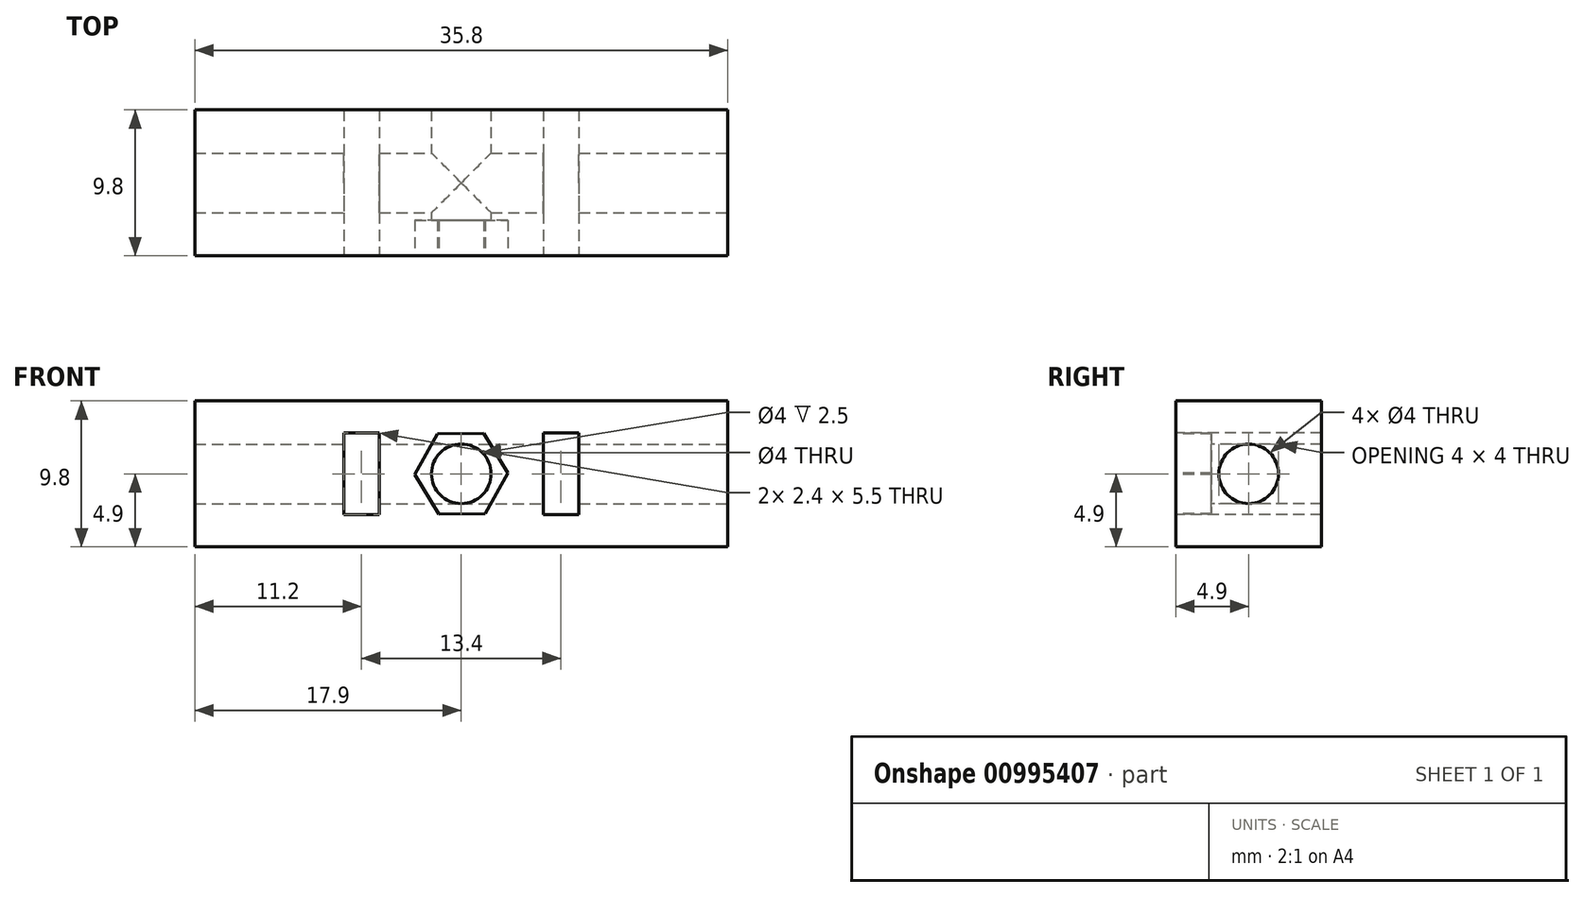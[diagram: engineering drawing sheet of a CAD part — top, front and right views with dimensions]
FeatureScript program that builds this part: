
annotation { "Feature Type Name" : "Feature", "Feature Type Description" : "" }
export const myFeature = defineFeature(function(context is Context, id is Id, definition is map)
    precondition{}
    {
        {
            var Q0;
            Q0=qCreatedBy(makeId("Front.planeOp"),FACE);
            var sketch = newSketch(context, id + "F0", { "sketchPlane" : qUnion([Q0])});
            skLineSegment(sketch, "E0.bottom", {"start": v(-17.9, 4.9) * mm, "end": v(17.9, 4.9) * mm});
            skLineSegment(sketch, "E0.top", {"start": v(-17.9, -4.9) * mm, "end": v(17.9, -4.9) * mm});
            skLineSegment(sketch, "E0.left", {"start": v(-17.9, 4.9) * mm, "end": v(-17.9, -4.9) * mm});
            skLineSegment(sketch, "E0.right", {"start": v(17.9, 4.9) * mm, "end": v(17.9, -4.9) * mm});
            skPoint(sketch, "E0.middle", {"position": v(0, 0) * mm});
            skSolve(sketch);
        }
        {
            var Q0;
            Q0=makeQuery(id+"F0.imprint","IMPRINT",FACE,{"disambiguationData":[TD([[makeQuery(id+"F0.imprint","IMPRINT",EDGE,{"derivedFrom":sQuery(id+"F0.wireOp",EDGE,"E0.bottom")}),-1.0]])]});
            extrude(context, id + "F1", {"entities" : qUnion([Q0]), "depth" : 9.8 * mm, "offsetDistance" : 25 * mm});
        }
        {
            var Q0;
            Q0=makeQuery(id+"F1.opExtrude","CAP_FACE",FACE,{"disambiguationData":[OSD([sQuery(id+"F0.wireOp",EDGE,"E0.bottom"),sQuery(id+"F0.wireOp",EDGE,"E0.top"),sQuery(id+"F0.wireOp",EDGE,"E0.left"),sQuery(id+"F0.wireOp",EDGE,"E0.right")])],"isStart":false});
            var sketch = newSketch(context, id + "F2", { "sketchPlane" : qUnion([Q0])});
            skCircle(sketch, "E1", {"center": v(0, 0) * mm, "radius": 2 * mm});
            skSolve(sketch);
        }
        {
            var Q0;
            Q0=makeQuery(id+"F2.imprint","IMPRINT",FACE,{"disambiguationData":[TD([[makeQuery(id+"F2.imprint","IMPRINT",EDGE,{"derivedFrom":sQuery(id+"F2.wireOp",EDGE,"E1")}),1.0]])]});
            extrude(context, id + "F3", {"entities" : qUnion([Q0]), "operationType" : NewBodyOperationType.REMOVE, "oppositeDirection" : true, "depth" : 25 * mm, "offsetDistance" : 25 * mm});
        }
        {
            var Q0;
            Q0=makeQuery(id+"F1.opExtrude","CAP_FACE",FACE,{"disambiguationData":[OSD([sQuery(id+"F0.wireOp",EDGE,"E0.bottom"),sQuery(id+"F0.wireOp",EDGE,"E0.top"),sQuery(id+"F0.wireOp",EDGE,"E0.left"),sQuery(id+"F0.wireOp",EDGE,"E0.right")])],"isStart":false});
            var sketch = newSketch(context, id + "F4", { "sketchPlane" : qUnion([Q0])});
            skCircle(sketch, "E2.cCircle", {"center": v(0, 0) * mm, "radius": 2.7 * mm, "construction": true});
            skLineSegment(sketch, "E2.0", {"start": v(-3.12, -0.05) * mm, "end": v(-1.6, 2.67) * mm});
            skLineSegment(sketch, "E2.1", {"start": v(-1.6, 2.67) * mm, "end": v(1.51, 2.73) * mm});
            skLineSegment(sketch, "E2.2", {"start": v(1.51, 2.73) * mm, "end": v(3.12, 0.05) * mm});
            skLineSegment(sketch, "E2.3", {"start": v(3.12, 0.05) * mm, "end": v(1.6, -2.67) * mm});
            skLineSegment(sketch, "E2.4", {"start": v(1.6, -2.67) * mm, "end": v(-1.51, -2.73) * mm});
            skLineSegment(sketch, "E2.5", {"start": v(-1.51, -2.73) * mm, "end": v(-3.12, -0.05) * mm});
            skPoint(sketch, "E2.0.midPoint", {"position": v(-2.36, 1.31) * mm});
            skSolve(sketch);
        }
        {
            var Q0;
            Q0=makeQuery(id+"F4.imprint","IMPRINT",FACE,{"disambiguationData":[TD([[makeQuery(id+"F4.imprint","IMPRINT",EDGE,{"derivedFrom":sQuery(id+"F4.wireOp",EDGE,"E2.0")}),-1.0]])]});
            extrude(context, id + "F5", {"entities" : qUnion([Q0]), "operationType" : NewBodyOperationType.REMOVE, "oppositeDirection" : true, "depth" : 2.4 * mm, "offsetDistance" : 25 * mm});
        }
        {
            var Q0;
            Q0=makeQuery(id+"F1.opExtrude","SWEPT_FACE",FACE,{"disambiguationData":[OSD([sQuery(id+"F0.wireOp",EDGE,"E0.right")])]});
            var sketch = newSketch(context, id + "F6", { "sketchPlane" : qUnion([Q0])});
            skCircle(sketch, "E3", {"center": v(-4.9, 0) * mm, "radius": 2 * mm});
            skSolve(sketch);
        }
        {
            var Q0;
            Q0=makeQuery(id+"F6.imprint","IMPRINT",FACE,{"disambiguationData":[TD([[makeQuery(id+"F6.imprint","IMPRINT",EDGE,{"derivedFrom":sQuery(id+"F6.wireOp",EDGE,"E3")}),1.0]])]});
            extrude(context, id + "F7", {"entities" : qUnion([Q0]), "operationType" : NewBodyOperationType.REMOVE, "oppositeDirection" : true, "depth" : 40 * mm, "offsetDistance" : 25 * mm});
        }
        {
            var Q0;
            Q0=makeQuery(id+"F1.opExtrude","CAP_FACE",FACE,{"disambiguationData":[OSD([sQuery(id+"F0.wireOp",EDGE,"E0.bottom"),sQuery(id+"F0.wireOp",EDGE,"E0.top"),sQuery(id+"F0.wireOp",EDGE,"E0.left"),sQuery(id+"F0.wireOp",EDGE,"E0.right")])],"isStart":false});
            var sketch = newSketch(context, id + "F8", { "sketchPlane" : qUnion([Q0])});
            skLineSegment(sketch, "E4.bottom", {"start": v(-7.9, 2.75) * mm, "end": v(-5.5, 2.75) * mm});
            skLineSegment(sketch, "E4.top", {"start": v(-7.9, -2.75) * mm, "end": v(-5.5, -2.75) * mm});
            skLineSegment(sketch, "E4.left", {"start": v(-7.9, 2.75) * mm, "end": v(-7.9, -2.75) * mm});
            skLineSegment(sketch, "E4.right", {"start": v(-5.5, 2.75) * mm, "end": v(-5.5, -2.75) * mm});
            skPoint(sketch, "E4.middle", {"position": v(-6.7, 0) * mm});
            skLineSegment(sketch, "E5.bottom", {"start": v(5.5, 2.75) * mm, "end": v(7.9, 2.75) * mm});
            skLineSegment(sketch, "E5.top", {"start": v(5.5, -2.75) * mm, "end": v(7.9, -2.75) * mm});
            skLineSegment(sketch, "E5.left", {"start": v(5.5, 2.75) * mm, "end": v(5.5, -2.75) * mm});
            skLineSegment(sketch, "E5.right", {"start": v(7.9, 2.75) * mm, "end": v(7.9, -2.75) * mm});
            skPoint(sketch, "E5.middle", {"position": v(6.7, 0) * mm});
            skSolve(sketch);
        }
        {
            var Q0;
            Q0=makeQuery(id+"F8.imprint","IMPRINT",FACE,{"disambiguationData":[TD([[makeQuery(id+"F8.imprint","IMPRINT",EDGE,{"derivedFrom":sQuery(id+"F8.wireOp",EDGE,"E5.bottom")}),-1.0]])]});
            var Q1;
            Q1=makeQuery(id+"F8.imprint","IMPRINT",FACE,{"disambiguationData":[TD([[makeQuery(id+"F8.imprint","IMPRINT",EDGE,{"derivedFrom":sQuery(id+"F8.wireOp",EDGE,"E4.bottom")}),-1.0]])]});
            extrude(context, id + "F9", {"entities" : qUnion([Q0, Q1]), "operationType" : NewBodyOperationType.REMOVE, "oppositeDirection" : true, "depth" : 25 * mm, "offsetDistance" : 25 * mm});
        }
    });
